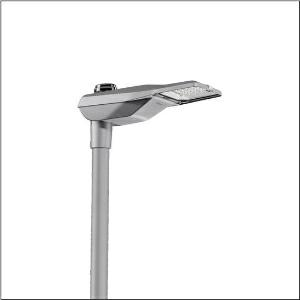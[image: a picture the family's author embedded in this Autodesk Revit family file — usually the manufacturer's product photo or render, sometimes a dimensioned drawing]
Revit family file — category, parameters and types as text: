
# Revit family: streetlight_sl_21_micro___pl52_5xe5h47n08cb_b1c0
name_source: partatom
category: Lighting Fixtures
units: mm (PartAtom-declared; Revit-internal decimal feet)

## family parameters
Cut with Voids When Loaded = No
Host = Face
Light Source = No
Part Type = Normal
Room Calculation Point = No
Round Connector Dimension = Use Diameter
Shared = No

## types (1)
- --- (1 x LED, 2340 lm, 15.8 W, 4000K)
    Apparent Load = 16 VA
    CIE Flux Codes = 27 59 98 100 100
    Color Rendering = 70
    Color Temperature = 4000K
    Default Elevation = 1800 mm
    Description = Streetlight SL 21 micro, mast luminaire, primary light control with lens, of PMMA, primary optical cover: cover, of toughened safety glass, transparent, light distribution: PL52, light emission: direct distribution, primary light characteristic: asymmetric, installation type: post-top, LED, 3G 1.5mm², High Power LED, rated luminous flux: 2.340lm, luminous efficacy: 148lm/W, light colour: 740, colour temperature: 4000K, control: overheat protection, pre-setting: linear dimming characteristic, constant luminous flux control, time-dependent luminous flux control, flexible luminous flux parameterisation, mains connection: 230..240V, AC, 50/60Hz, connection cable pre-assembled, cable length: 6,5m, wiring characteristics: H07RN-F, start of lifetime: 16W, end of service life: 16W, reduction: 8W, luminaire housing, of diecast aluminium (EN AC-44300), powder-coated, Siteco® metallic grey (DB 702S), corrosivity category C5 mid according to DIN EN ISO 12944, multi-level sealing system, sealing non-destructively replaceable, inclination adjustable: 0°, 5°, 10°, 15°, length: 528mm, width: 235mm, height: 110mm, spigot size: 76/60mm (post-top), protection rating (complete): IP66, insulation class (complete): insulation class I (protective earthing), certification: CE, ENEC, ENEC+, VDE, impact resistance: IK09, permissible operating ambient temperature for outdoor applications: -40..+50°C, standard-compliant lighting for roads and squares, packaging unit: 1 piece

Light Distribution: PL52
    Height = 110 mm
    Lamp = 1 x LED
    Lamp Light Flux = 2340 lm
    Lamp Power = 15.8 W
    Lamp count = 1
    Length = 528 mm
    Luminous efficacy = 148 lm/W
    Manufacturer = Siteco
    ModVariant = No
    Model = 5XE5H47N08CB
    Number of Poles = 1
    OnlyDefault = Yes
    Power Factor = 1
    Product Name = Streetlight SL 21 micro | PL52
    Product group = mast luminaire | pylon top
    ProductGroupID = 6100
    Protection Class = Protection class I
    Protection Degree = IP 66
    RLX_Detail_Level = 1
    RLX_Emergency_Light_Flux = 0 lm
    RLX_Emergency_Type = 0
    RLX_Emergency_Type_DB = No
    RlxData = <blob elided: 108449 chars, md5=09104014>
    Socket = socket
    Standby Power = 0 W
    System Light Flux = 2340 lm
    System Power = 16 W
    Type Comments = factory setting: luminous flux: 100 % | dim-lin: 254 | 300 mA
    Type Image = l_1294375.jpg
    URL = http://relux.com
    VarID = @adj_106963
    Voltage = 0 V
    Weight = 0.00 kg
    Width = 235 mm

## geometry (parser evidence)
native form markers: Blend x4, Sweep x12
no freeform markers — native parametric forms only
